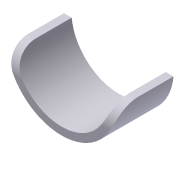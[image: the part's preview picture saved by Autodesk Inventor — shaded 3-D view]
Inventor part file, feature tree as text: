
AUTODESK INVENTOR PART (.ipt)
format: ipt  version: 2012 (Build 160160000, 160)  size: 88,064 bytes
history: native  units: in
note: dims shown in document units (in); Inventor stores cm internally (conversion verified against a paired STEP export)
features: extrude x1, fillet x1, sketch x1
ambient origin geometry x8: Origin, YZ Plane, XZ Plane, XY Plane, X Axis, Y Axis, Z Axis, Center Point
bodies: Solid1 (feature_tree)
feature tree (3):
  extrude  "Extrusion1"  Depth=0.828in
  fillet  "Fillet1"  Radius=0.9625in
  sketch  "Sketch1"  dims[d0=0.875in d1=0.828in d2=0.9625in d3=1.0in d4=0.0in d5=0.375in]
